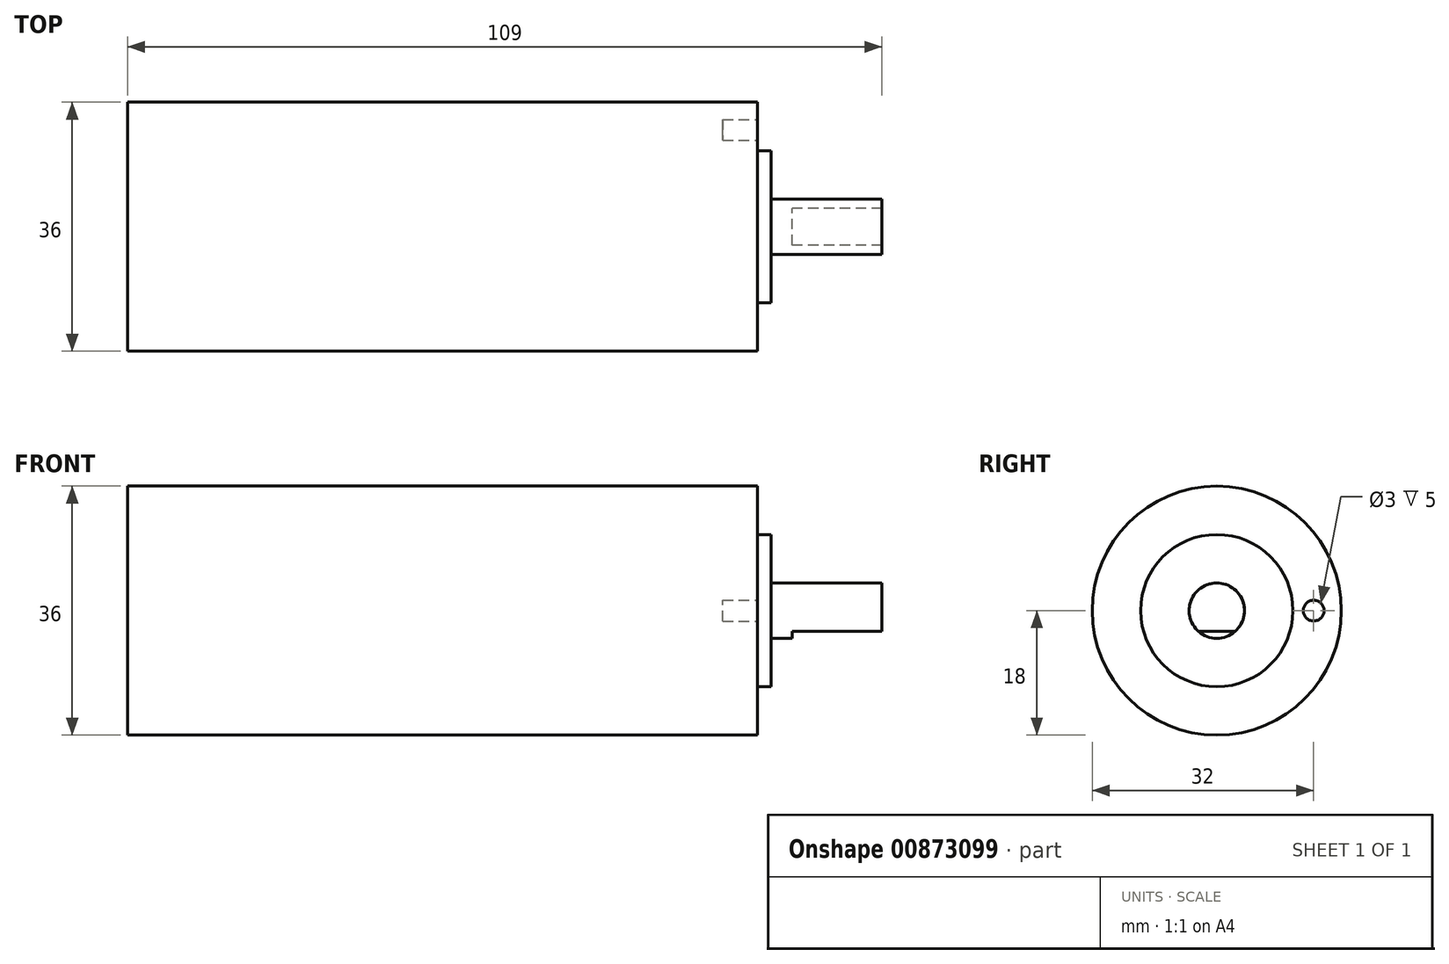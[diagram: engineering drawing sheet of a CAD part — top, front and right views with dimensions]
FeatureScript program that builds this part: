
annotation { "Feature Type Name" : "Feature", "Feature Type Description" : "" }
export const myFeature = defineFeature(function(context is Context, id is Id, definition is map)
    precondition{}
    {
        {
            var Q0;
            Q0=qCreatedBy(makeId("Right.planeOp"),FACE);
            var sketch = newSketch(context, id + "F0", { "sketchPlane" : qUnion([Q0])});
            skCircle(sketch, "E0", {"center": v(0, 0) * mm, "radius": 18 * mm});
            skSolve(sketch);
        }
        {
            var Q0;
            Q0=makeQuery(id+"F0.imprint","IMPRINT",FACE,{"disambiguationData":[TD([[makeQuery(id+"F0.imprint","IMPRINT",EDGE,{"derivedFrom":sQuery(id+"F0.wireOp",EDGE,"E0")}),1.0]])]});
            extrude(context, id + "F1", {"entities" : qUnion([Q0]), "oppositeDirection" : true, "offsetDistance" : 25 * mm, "depth" : 91 * mm});
        }
        {
            var Q0;
            Q0=qCreatedBy(makeId("Right.planeOp"),FACE);
            var sketch = newSketch(context, id + "F2", { "sketchPlane" : qUnion([Q0])});
            skCircle(sketch, "E1", {"center": v(0, 0) * mm, "radius": 11 * mm});
            skSolve(sketch);
        }
        {
            var Q0;
            Q0=makeQuery(id+"F2.imprint","IMPRINT",FACE,{"disambiguationData":[TD([[makeQuery(id+"F2.imprint","IMPRINT",EDGE,{"derivedFrom":sQuery(id+"F2.wireOp",EDGE,"E1")}),1.0]])]});
            extrude(context, id + "F3", {"entities" : qUnion([Q0]), "operationType" : NewBodyOperationType.ADD, "offsetDistance" : 25 * mm, "depth" : 2 * mm});
        }
        {
            var Q0;
            Q0=qCreatedBy(makeId("Right.planeOp"),FACE);
            var sketch = newSketch(context, id + "F4", { "sketchPlane" : qUnion([Q0])});
            skCircle(sketch, "E2", {"center": v(0, 0) * mm, "radius": 4 * mm});
            skSolve(sketch);
        }
        {
            var Q0;
            Q0=qSketchRegion(id+"F4",true);
            extrude(context, id + "F5", {"entities" : qUnion([Q0]), "operationType" : NewBodyOperationType.ADD, "offsetDistance" : 25 * mm, "depth" : 18 * mm});
        }
        {
            var Q0;
            Q0=qCreatedBy(makeId("Right.planeOp"),FACE);
            var sketch = newSketch(context, id + "F6", { "sketchPlane" : qUnion([Q0])});
            skCircle(sketch, "E3", {"center": v(14, 0) * mm, "radius": 1.5 * mm});
            skSolve(sketch);
        }
        {
            var Q0;
            Q0=qSketchRegion(id+"F6",true);
            extrude(context, id + "F7", {"entities" : qUnion([Q0]), "operationType" : NewBodyOperationType.REMOVE, "oppositeDirection" : true, "depth" : 5 * mm});
        }
        {
            var Q0;
            Q0=qCreatedBy(makeId("Right.planeOp"),FACE);
            var sketch = newSketch(context, id + "F8", { "sketchPlane" : qUnion([Q0])});
            skLineSegment(sketch, "E4.bottom", {"start": v(-10, -3) * mm, "end": v(10, -3) * mm});
            skLineSegment(sketch, "E4.top", {"start": v(-10, -13) * mm, "end": v(10, -13) * mm});
            skLineSegment(sketch, "E4.left", {"start": v(-10, -3) * mm, "end": v(-10, -13) * mm});
            skLineSegment(sketch, "E4.right", {"start": v(10, -13) * mm, "end": v(10, -3) * mm});
            skSolve(sketch);
        }
        {
            var Q0;
            Q0=makeQuery(id+"F8.imprint","IMPRINT",FACE,{"disambiguationData":[TD([[makeQuery(id+"F8.imprint","IMPRINT",EDGE,{"derivedFrom":sQuery(id+"F8.wireOp",EDGE,"E4.bottom")}),-1.0]])]});
            extrude(context, id + "F9", {"entities" : qUnion([Q0]), "operationType" : NewBodyOperationType.REMOVE, "offsetDistance" : 25 * mm, "depth" : 25 * mm, "hasSecondDirection" : true, "secondDirectionOppositeDirection" : false, "secondDirectionDepth" : 5 * mm});
        }
    });
